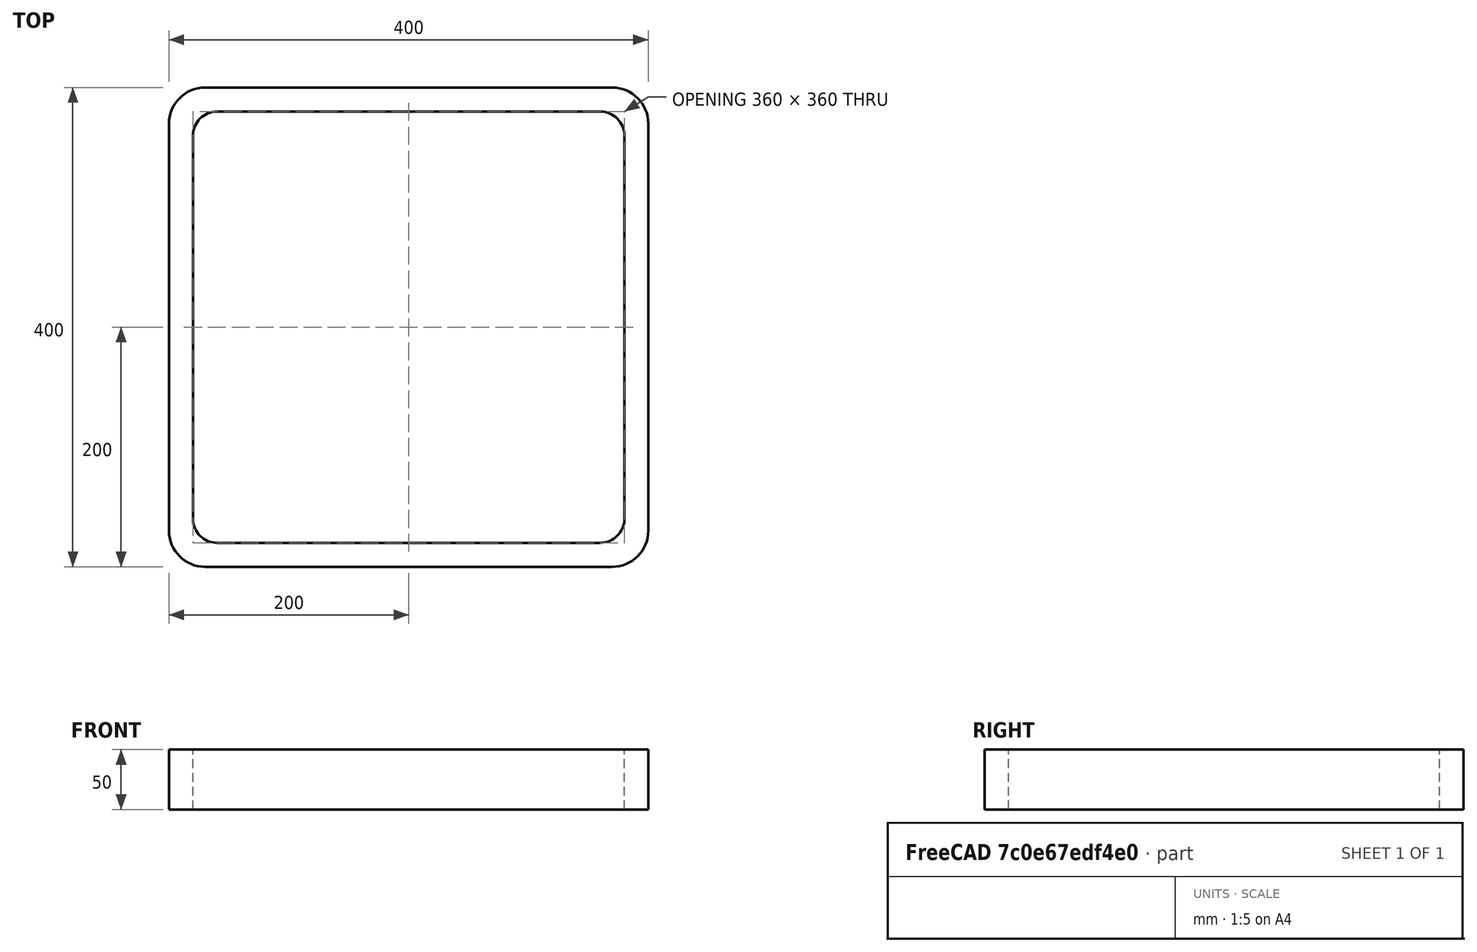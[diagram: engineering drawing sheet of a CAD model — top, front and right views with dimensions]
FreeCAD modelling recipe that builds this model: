
FCSTD DOCUMENT  (FreeCAD 0.15R4671 (Git))
Label: Square hollow section 400x400x20 EN10219 S235JRH
License: All rights reserved
LicenseURL: http://en.wikipedia.org/wiki/All_rights_reserved
objects: Sketcher::SketchObject×1, Part::Extrusion×1
note: 2 computed .brp shape members not serialized (recipe doc carries the construction recipe); baked Part::Feature solids carry a one-line shape summary decoded from their .brp

FEATURE [Sketcher::SketchObject] Sketch
  sketch-geometry (16):
    g0: LineSegment StartX=-160 StartY=180 StartZ=0 EndX=160 EndY=180 EndZ=0
    g1: LineSegment StartX=180 StartY=160 StartZ=0 EndX=180 EndY=-160 EndZ=0
    g2: LineSegment StartX=160 StartY=-180 StartZ=0 EndX=-160 EndY=-180 EndZ=0
    g3: LineSegment StartX=-180 StartY=-160 StartZ=0 EndX=-180 EndY=160 EndZ=0
    g4: LineSegment StartX=-170 StartY=200 StartZ=0 EndX=170 EndY=200 EndZ=0
    g5: LineSegment StartX=200 StartY=170 StartZ=0 EndX=200 EndY=-170 EndZ=0
    g6: LineSegment StartX=170 StartY=-200 StartZ=0 EndX=-170 EndY=-200 EndZ=0
    g7: LineSegment StartX=-200 StartY=-170 StartZ=0 EndX=-200 EndY=170 EndZ=0
    g8: ArcOfCircle CenterX=-160 CenterY=160 CenterZ=0 NormalX=0 NormalY=0 NormalZ=1 Radius=20 StartAngle=1.5708 EndAngle=3.14159
    g9: ArcOfCircle CenterX=160 CenterY=160 CenterZ=0 NormalX=0 NormalY=0 NormalZ=1 Radius=20 StartAngle=0 EndAngle=1.5708
    g10: ArcOfCircle CenterX=160 CenterY=-160 CenterZ=0 NormalX=0 NormalY=0 NormalZ=1 Radius=20 StartAngle=4.71239 EndAngle=6.28319
    g11: ArcOfCircle CenterX=-160 CenterY=-160 CenterZ=0 NormalX=0 NormalY=0 NormalZ=1 Radius=20 StartAngle=3.14159 EndAngle=4.71239
    g12: ArcOfCircle CenterX=170 CenterY=170 CenterZ=0 NormalX=0 NormalY=0 NormalZ=1 Radius=30 StartAngle=0 EndAngle=1.5708
    g13: ArcOfCircle CenterX=170 CenterY=-170 CenterZ=0 NormalX=0 NormalY=0 NormalZ=1 Radius=30 StartAngle=4.71239 EndAngle=6.28319
    g14: ArcOfCircle CenterX=-170 CenterY=-170 CenterZ=0 NormalX=0 NormalY=0 NormalZ=1 Radius=30 StartAngle=3.14159 EndAngle=4.71239
    g15: ArcOfCircle CenterX=-170 CenterY=170 CenterZ=0 NormalX=0 NormalY=0 NormalZ=1 Radius=30 StartAngle=1.5708 EndAngle=3.14159
  constraints (36):
    c: Horizontal(g2)
    c: Vertical(g3)
    c: Horizontal(g6)
    c: Vertical(g7)
    c: Tangent(g3,g8) = 1.5708
    c: Tangent(g0,g8) = 1.5708
    c: Tangent(g0,g9) = 1.5708
    c: Tangent(g1,g9) = 1.5708
    c: Tangent(g1,g10) = 1.5708
    c: Tangent(g2,g10) = 1.5708
    c: Tangent(g2,g11) = 1.5708
    c: Tangent(g3,g11) = 1.5708
    c: Tangent(g4,g12) = 1.5708
    c: Tangent(g5,g12) = 1.5708
    c: Tangent(g5,g13) = 1.5708
    c: Tangent(g6,g13) = 1.5708
    c: Tangent(g6,g14) = 1.5708
    c: Tangent(g7,g14) = 1.5708
    c: Tangent(g7,g15) = 1.5708
    c: Tangent(g4,g15) = 1.5708
    c: Equal(g9,g8)
    c: Equal(g9,g11)
    c: Equal(g9,g10)
    c: Equal(g12,g15)
    c: Equal(g12,g14)
    c: Equal(g12,g13)
    c: Symmetric(g4,g6,g-1)
    c: Symmetric(g7,g5,g-2)
    c: DistanceY(g4,g6) = -400
    c: DistanceX(g7,g5) = 400
    c: Symmetric(g3,g1,g-2)
    c: Symmetric(g0,g2,g-1)
    c: DistanceY(g0,g4) = 20
    c: DistanceX(g5,g1) = -20
    c: Radius(g9) = 20
    c: Radius(g12) = 30
FEATURE [Part::Extrusion] Extrude  label="Square hollow section 400x400x20 EN10219 S235JRH"
  Base = -> Sketch
  Dir = (0,0,50)
  Solid = true
